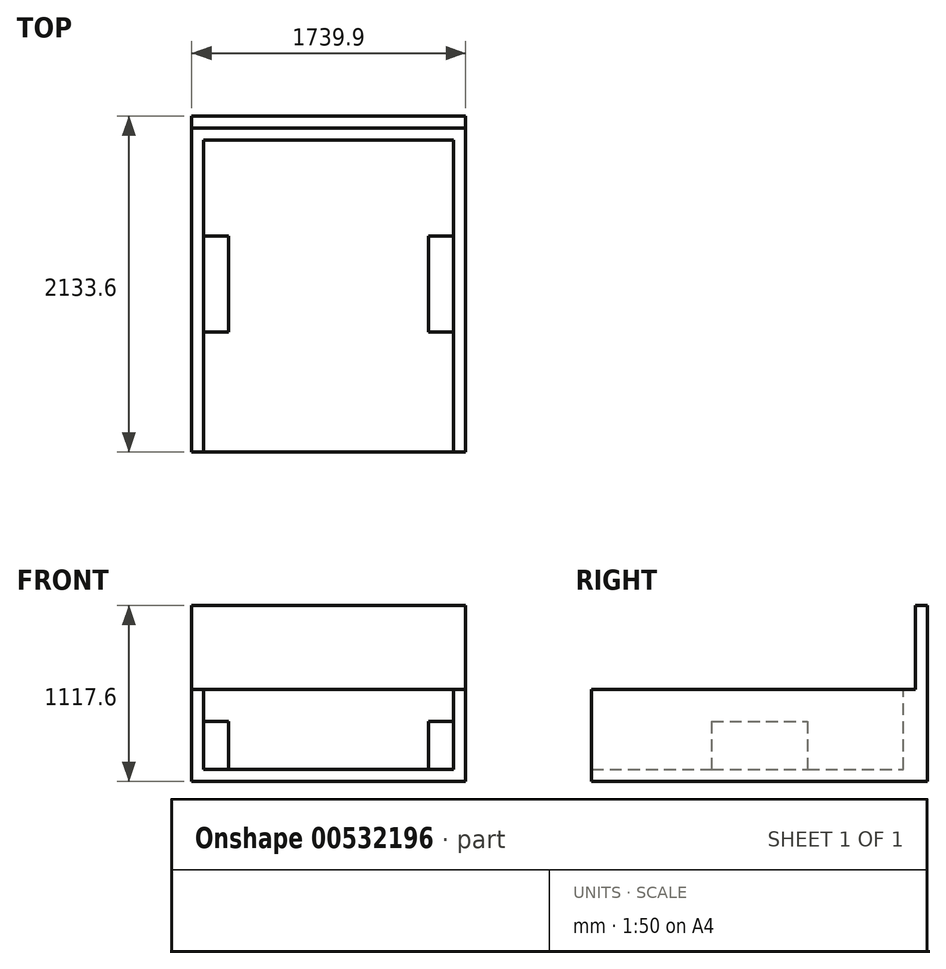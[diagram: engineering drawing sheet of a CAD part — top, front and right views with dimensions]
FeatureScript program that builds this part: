
annotation { "Feature Type Name" : "Feature", "Feature Type Description" : "" }
export const myFeature = defineFeature(function(context is Context, id is Id, definition is map)
    precondition{}
    {
        {
            var Q0;
            Q0=qCreatedBy(makeId("Front.planeOp"),FACE);
            var sketch = newSketch(context, id + "F0", { "sketchPlane" : qUnion([Q0])});
            skLineSegment(sketch, "E0.bottom", {"start": v(869.95, 292.1) * mm, "end": v(793.75, 292.1) * mm});
            skLineSegment(sketch, "E0.top", {"start": v(869.95, -292.1) * mm, "end": v(-869.95, -292.1) * mm});
            skLineSegment(sketch, "E0.left", {"start": v(869.95, 292.1) * mm, "end": v(869.95, -292.1) * mm});
            skLineSegment(sketch, "E0.right", {"start": v(-869.95, 292.1) * mm, "end": v(-869.95, -292.1) * mm});
            skPoint(sketch, "E0.middle", {"position": v(0, 0) * mm});
            skLineSegment(sketch, "E1", {"start": v(-793.75, 292.1) * mm, "end": v(-793.75, -215.9) * mm});
            skLineSegment(sketch, "E2", {"start": v(-793.75, -215.9) * mm, "end": v(793.75, -215.9) * mm});
            skLineSegment(sketch, "E3", {"start": v(793.75, -215.9) * mm, "end": v(793.75, 292.1) * mm});
            skPoint(sketch, "E4", {"position": v(0, -215.9) * mm});
            skLineSegment(sketch, "E5", {"start": v(-793.75, 292.1) * mm, "end": v(-869.95, 292.1) * mm});
            skLineSegment(sketch, "E6", {"start": v(793.75, 292.1) * mm, "end": v(-793.75, 292.1) * mm, "construction": true});
            skSolve(sketch);
        }
        {
            var Q0;
            Q0 = qSketchRegion(id + "F0", true);
            extrude(context, id + "F1", {"entities" : qUnion([Q0]), "depth" : 1981.2 * mm, "offsetDistance" : 25.4 * mm});
        }
        {
            var Q0;
            Q0=makeQuery(id+"F1.opExtrude","CAP_FACE",FACE,{"disambiguationData":[OSD([sQuery(id+"F0.wireOp",EDGE,"E0.bottom"),sQuery(id+"F0.wireOp",EDGE,"E0.top"),sQuery(id+"F0.wireOp",EDGE,"E0.left"),sQuery(id+"F0.wireOp",EDGE,"E0.right"),sQuery(id+"F0.wireOp",EDGE,"E1"),sQuery(id+"F0.wireOp",EDGE,"E2"),sQuery(id+"F0.wireOp",EDGE,"E3"),sQuery(id+"F0.wireOp",EDGE,"E5")])],"isStart":true});
            var sketch = newSketch(context, id + "F2", { "sketchPlane" : qUnion([Q0])});
            skLineSegment(sketch, "E7.bottom", {"start": v(-869.95, 292.1) * mm, "end": v(869.95, 292.1) * mm});
            skLineSegment(sketch, "E7.top", {"start": v(-869.95, -292.1) * mm, "end": v(869.95, -292.1) * mm});
            skLineSegment(sketch, "E7.left", {"start": v(-869.95, 292.1) * mm, "end": v(-869.95, -292.1) * mm});
            skLineSegment(sketch, "E7.right", {"start": v(869.95, 292.1) * mm, "end": v(869.95, -292.1) * mm});
            skSolve(sketch);
        }
        {
            var Q0;
            Q0 = qSketchRegion(id + "F2", true);
            extrude(context, id + "F3", {"entities" : qUnion([Q0]), "operationType" : NewBodyOperationType.ADD, "depth" : 76.2 * mm, "offsetDistance" : 25.4 * mm});
        }
        {
            var Q0;
            Q0=makeQuery(id+"F1.opExtrude","SWEPT_FACE",FACE,{"disambiguationData":[OSD([sQuery(id+"F0.wireOp",EDGE,"E2")])]});
            var sketch = newSketch(context, id + "F4", { "sketchPlane" : qUnion([Q0])});
            skLineSegment(sketch, "E8.bottom", {"start": v(-793.75, -1219.2) * mm, "end": v(-635, -1219.2) * mm});
            skLineSegment(sketch, "E8.top", {"start": v(-793.75, -609.6) * mm, "end": v(-635, -609.6) * mm});
            skLineSegment(sketch, "E8.left", {"start": v(-793.75, -1219.2) * mm, "end": v(-793.75, -609.6) * mm});
            skLineSegment(sketch, "E8.right", {"start": v(-635, -1219.2) * mm, "end": v(-635, -609.6) * mm});
            skLineSegment(sketch, "E9.bottom", {"start": v(793.75, -1219.2) * mm, "end": v(635, -1219.2) * mm});
            skLineSegment(sketch, "E9.top", {"start": v(793.75, -609.6) * mm, "end": v(635, -609.6) * mm});
            skLineSegment(sketch, "E9.left", {"start": v(793.75, -1219.2) * mm, "end": v(793.75, -609.6) * mm});
            skLineSegment(sketch, "E9.right", {"start": v(635, -1219.2) * mm, "end": v(635, -609.6) * mm});
            skSolve(sketch);
        }
        {
            var Q0;
            Q0 = qSketchRegion(id + "F4", true);
            extrude(context, id + "F5", {"entities" : qUnion([Q0]), "operationType" : NewBodyOperationType.ADD, "depth" : 304.8 * mm, "offsetDistance" : 25.4 * mm});
        }
        {
            var Q0;
            Q0=makeQuery(id+"F3.opExtrude","CAP_FACE",FACE,{"disambiguationData":[OSD([sQuery(id+"F2.wireOp",EDGE,"E7.bottom"),sQuery(id+"F2.wireOp",EDGE,"E7.top"),sQuery(id+"F2.wireOp",EDGE,"E7.left"),sQuery(id+"F2.wireOp",EDGE,"E7.right")])],"isStart":false});
            var sketch = newSketch(context, id + "F6", { "sketchPlane" : qUnion([Q0])});
            skLineSegment(sketch, "E10.bottom", {"start": v(-869.95, -292.1) * mm, "end": v(869.95, -292.1) * mm});
            skLineSegment(sketch, "E10.top", {"start": v(-869.95, 825.5) * mm, "end": v(869.95, 825.5) * mm});
            skLineSegment(sketch, "E10.left", {"start": v(-869.95, -292.1) * mm, "end": v(-869.95, 825.5) * mm});
            skLineSegment(sketch, "E10.right", {"start": v(869.95, -292.1) * mm, "end": v(869.95, 825.5) * mm});
            skSolve(sketch);
        }
        {
            var Q0;
            Q0 = qSketchRegion(id + "F6", true);
            extrude(context, id + "F7", {"entities" : qUnion([Q0]), "operationType" : NewBodyOperationType.ADD, "depth" : 76.2 * mm, "offsetDistance" : 25.4 * mm});
        }
    });
